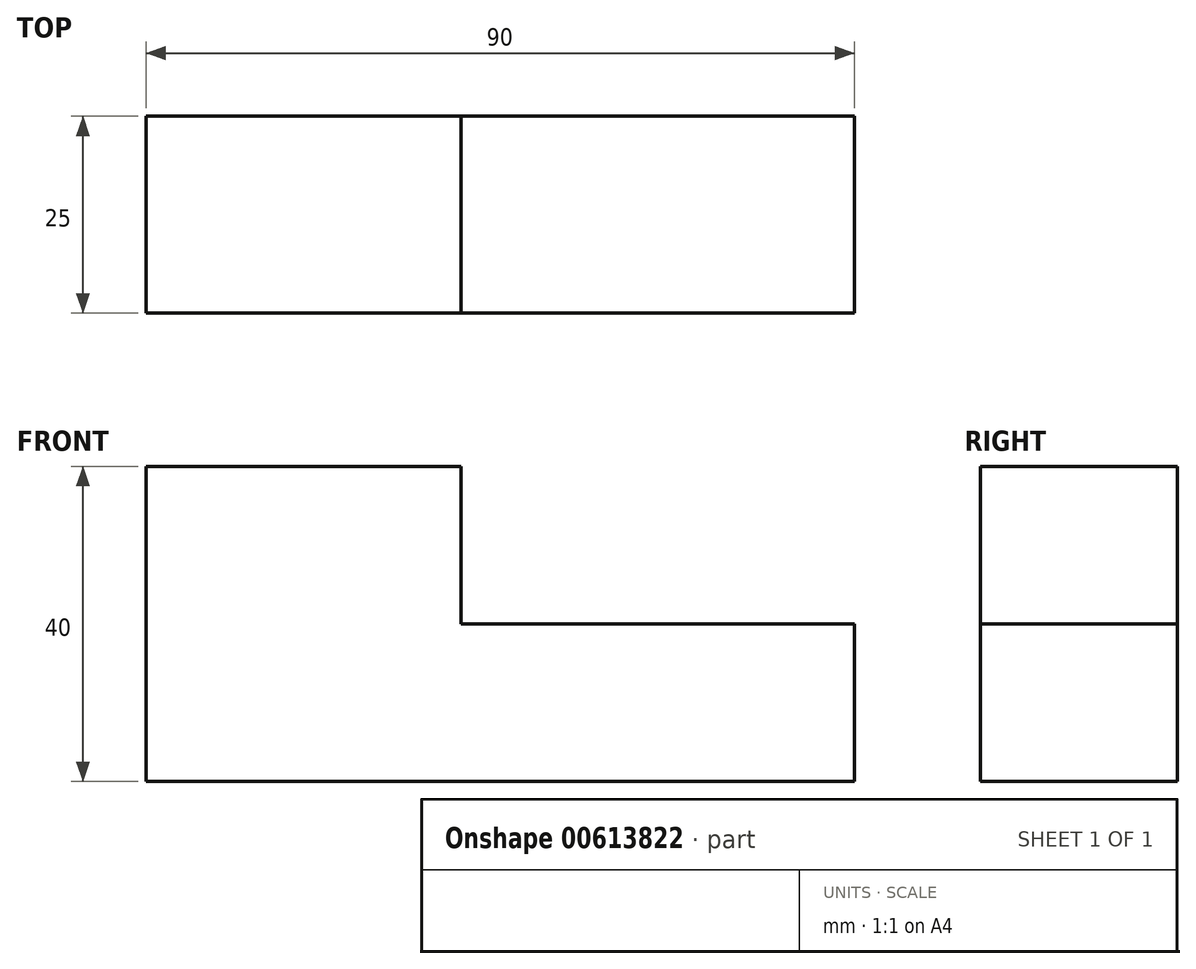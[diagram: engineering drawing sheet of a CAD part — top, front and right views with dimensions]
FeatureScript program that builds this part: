
annotation { "Feature Type Name" : "Feature", "Feature Type Description" : "" }
export const myFeature = defineFeature(function(context is Context, id is Id, definition is map)
    precondition{}
    {
        {
            var Q0;
            Q0=qCreatedBy(makeId("Front.planeOp"),FACE);
            var sketch = newSketch(context, id + "F0", { "sketchPlane" : qUnion([Q0])});
            skLineSegment(sketch, "E0", {"start": v(-56.17, 52.01) * mm, "end": v(-16.17, 52.01) * mm});
            skLineSegment(sketch, "E1", {"start": v(-16.17, 52.01) * mm, "end": v(-16.17, 32.01) * mm});
            skLineSegment(sketch, "E2", {"start": v(-16.17, 32.01) * mm, "end": v(33.83, 32.01) * mm});
            skLineSegment(sketch, "E3", {"start": v(33.83, 32.01) * mm, "end": v(33.83, 12.01) * mm});
            skLineSegment(sketch, "E4", {"start": v(33.83, 12.01) * mm, "end": v(-56.17, 12.01) * mm});
            skLineSegment(sketch, "E5", {"start": v(-56.17, 12.01) * mm, "end": v(-56.17, 52.01) * mm});
            skSolve(sketch);
        }
        {
            var Q0;
            Q0 = qSketchRegion(id + "F0", true);
            extrude(context, id + "F1", {"entities" : qUnion([Q0]), "depth" : 25 * mm, "offsetDistance" : 25 * mm});
        }
    });
